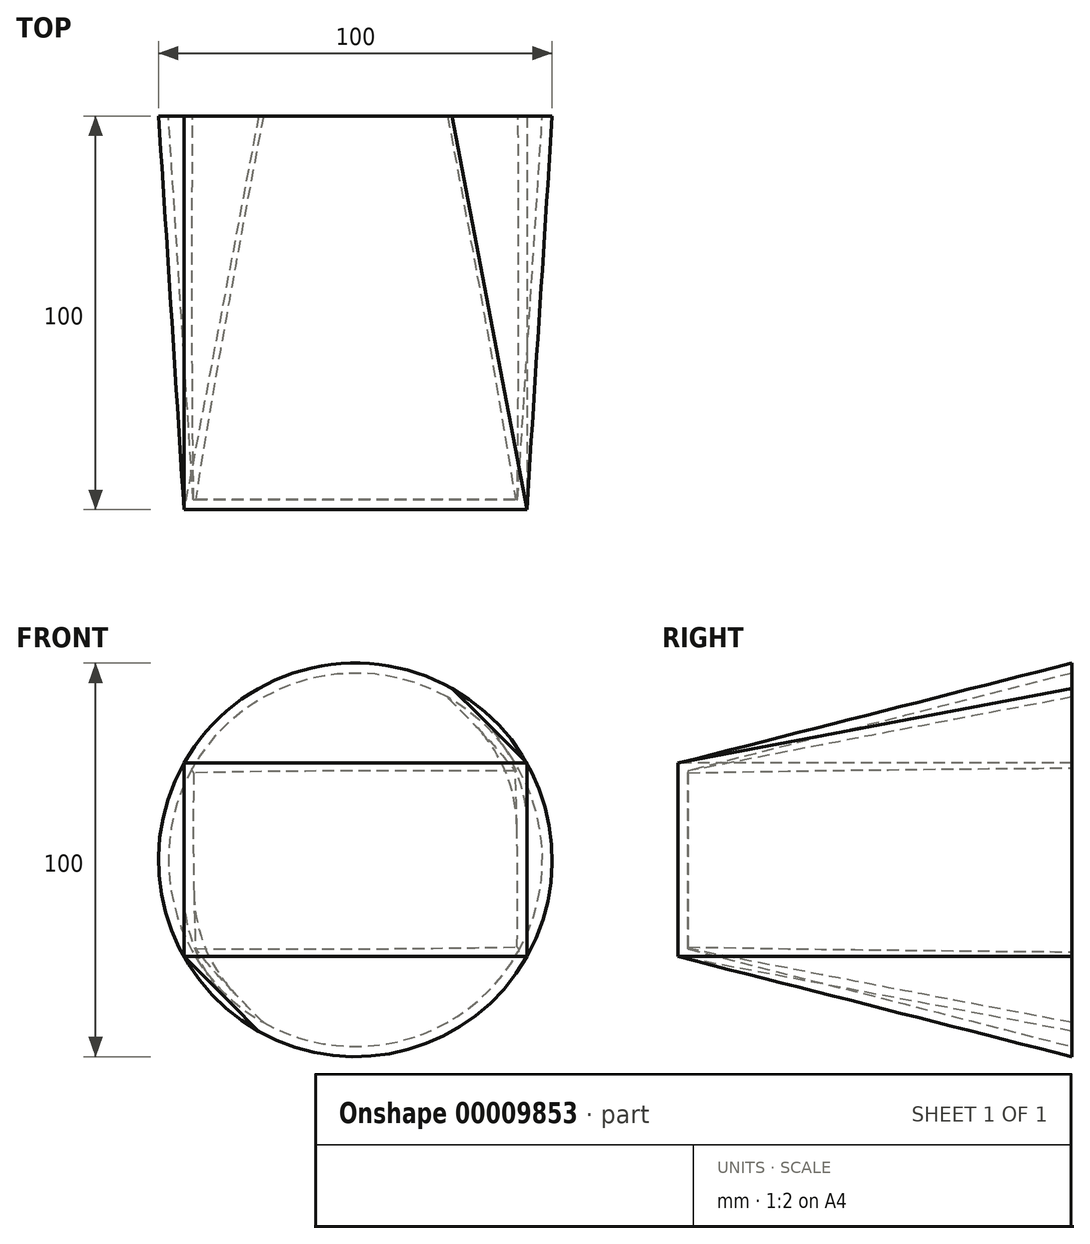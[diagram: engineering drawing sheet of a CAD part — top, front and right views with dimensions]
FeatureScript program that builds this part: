
annotation { "Feature Type Name" : "Feature", "Feature Type Description" : "" }
export const myFeature = defineFeature(function(context is Context, id is Id, definition is map)
    precondition{}
    {
        {
            var Q0;
            Q0=qCreatedBy(makeId("Front.planeOp"),FACE);
            var sketch = newSketch(context, id + "F0", { "sketchPlane" : qUnion([Q0])});
            skCircle(sketch, "E0", {"center": v(0, 0) * mm, "radius": 50 * mm});
            skSolve(sketch);
        }
        {
            var Q0;
            Q0=qCreatedBy(makeId("Front.planeOp"),FACE);
            cPlane(context, id + "F1", {"entities" : qUnion([Q0]), "cplaneType" : CPlaneType.OFFSET, "offset" : 100 * mm, "width" : 150 * mm, "height" : 150 * mm});
        }
        {
            var Q0;
            Q0=qCreatedBy(id+"F1.planeOp",FACE);
            var sketch = newSketch(context, id + "F2", { "sketchPlane" : qUnion([Q0])});
            skLineSegment(sketch, "E1.rect.bottom", {"start": v(-43.54, 24.58) * mm, "end": v(43.54, 24.58) * mm});
            skLineSegment(sketch, "E1.rect.top", {"start": v(-43.54, -24.58) * mm, "end": v(43.54, -24.58) * mm});
            skLineSegment(sketch, "E1.rect.left", {"start": v(-43.54, 24.58) * mm, "end": v(-43.54, -24.58) * mm});
            skLineSegment(sketch, "E1.rect.right", {"start": v(43.54, 24.58) * mm, "end": v(43.54, -24.58) * mm});
            skPoint(sketch, "E1.rect.middle", {"position": v(0, 0) * mm});
            skSolve(sketch);
        }
        {
            var Q0;
            Q0 = qSketchRegion(id + "F0", true);
            var Q1;
            Q1 = qSketchRegion(id + "F2", true);
            loft(context, id + "F3", {"sheetProfilesArray" : [{ "sheetProfileEntities" : qUnion([Q0]) }, { "sheetProfileEntities" : qUnion([Q1]) }]});
        }
        {
            var Q0;
            Q0=makeQuery(id+"F3.opLoft","CAP_FACE",FACE,{"disambiguationData":[OSD([makeQuery(id+"F0.imprint","IMPRINT",FACE,{"disambiguationData":[TD([[makeQuery(id+"F0.imprint","IMPRINT",EDGE,{"derivedFrom":sQuery(id+"F0.wireOp",EDGE,"E0")}),1.0]])]})])],"isStart":true});
            shell(context, id + "F4", {"entities" : qUnion([Q0]), "thickness" : 2.5 * mm});
        }
    });
